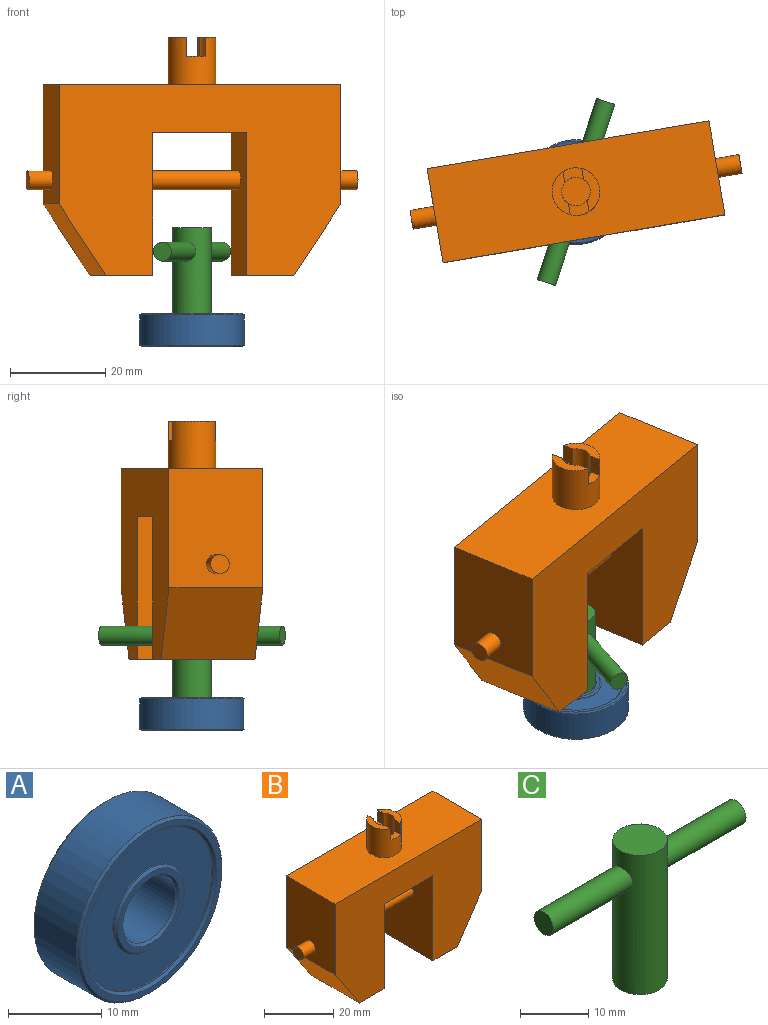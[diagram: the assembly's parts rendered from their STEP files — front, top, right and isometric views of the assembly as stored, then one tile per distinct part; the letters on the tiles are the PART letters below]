
ASSEMBLY  parts=3 mates=2
PART A: 20 faces, bbox 22x7x22 mm
  f0: cylinder r=9.7mm len=19.4mm, axis (0,1,0), area 12.2mm2, adj f11,f14
  f1: cylinder r=9.7mm len=19.4mm, axis (0,1,0), area 12.2mm2, adj f10,f18
  f2: cylinder r=11mm len=22mm, axis (0,1,0), area 442.3mm2, adj f15,f19
  f3: plane 21.4x21.4mm, normal (0,-1,0), area 45.5mm2, adj f18,f19
  f4: plane 21.4x21.4mm, normal (0,1,0), area 45.5mm2, adj f14,f15
  f5: cylinder r=5.3mm len=10.6mm, axis (0,1,0), area 6.7mm2, adj f11,f13
  f6: cylinder r=4mm len=8mm, axis (0,1,0), area 160.8mm2, adj f12,f16
  f7: cylinder r=5.3mm len=10.6mm, axis (0,1,0), area 6.7mm2, adj f10,f17
  f8: plane 10x10mm, normal (0,-1,0), area 20.5mm2, adj f16,f17
  f9: plane 10x10mm, normal (0,1,0), area 20.5mm2, adj f12,f13
  f10: plane 19.4x19.4mm, normal (0,-1,0), area 207.3mm2, adj f1,f7
  f11: plane 19.4x19.4mm, normal (0,1,0), area 207.3mm2, adj f0,f5
  f12: cone r=4.3mm half-angle=45deg, axis (0,1,0), area 11.1mm2, adj f6,f9
  f13: cone r=5.3mm half-angle=45deg, axis (0,-1,0), area 13.7mm2, adj f5,f9
  f14: cone r=10mm half-angle=45deg, axis (0,1,0), area 26.3mm2, adj f0,f4
  f15: cone r=11mm half-angle=45deg, axis (0,-1,0), area 28.9mm2, adj f2,f4
  f16: cone r=4mm half-angle=45deg, axis (0,-1,0), area 11.1mm2, adj f6,f8
  f17: cone r=5mm half-angle=45deg, axis (0,1,0), area 13.7mm2, adj f7,f8
  f18: cone r=9.7mm half-angle=45deg, axis (0,-1,0), area 26.3mm2, adj f1,f3
  f19: cone r=10.7mm half-angle=45deg, axis (0,1,0), area 28.9mm2, adj f2,f3
PART B: 28 faces, bbox 70x20x50 mm
  f0: cylinder r=3mm len=10mm, axis (0,0,-1), area 153.5mm2, adj f2,f20,f21,f22,f23,f24,f25,f26
  f1: cylinder r=5mm len=10mm, axis (0,0,-1), area 281.2mm2, adj f2,f10,f20,f22,f23,f24,f25,f26
  f2: plane 9.17x3mm, normal (0,0,1), area 16.7mm2, adj f0,f1,f24,f26
  f3: plane 20x10mm, normal (0,0,-1), area 200mm2, adj f4,f12,f13,f14
  f4: plane 30x20mm, normal (1,0,0), area 587.4mm2, adj f3,f5,f13,f14,f19
  f5: plane 20x20mm, normal (0,0,-1), area 400mm2, adj f4,f6,f13,f14
  f6: plane 30x20mm, normal (-1,0,0), area 587.4mm2, adj f5,f7,f13,f14,f19
  f7: plane 20x10mm, normal (0,0,-1), area 200mm2, adj f6,f8,f13,f14
  f8: plane 20x15mm, normal (0.83,0,-0.55), area 360.6mm2, adj f7,f9,f13,f14
  f9: plane 25x20mm, normal (1,0,0), area 487.4mm2, adj f8,f10,f13,f14,f18
  f10: plane 60x20mm, normal (0,0,1), area 1121.5mm2, adj f1,f9,f11,f13,f14
  f11: plane 25x20mm, normal (-1,0,0), area 487.4mm2, adj f10,f12,f13,f14,f16
  f12: plane 20x15mm, normal (-0.83,0,-0.55), area 360.6mm2, adj f3,f11,f13,f14
  f13: plane 60x40mm, normal (0,-1,0), area 1650mm2, adj f3,f4,f5,f6,f7,f8,f9,f10
  f14: plane 60x40mm, normal (0,1,0), area 1650mm2, adj f3,f4,f5,f6,f7,f8,f9,f10
  f15: plane 4x4mm, normal (-1,0,0), area 12.6mm2, adj f16
  f16: cylinder r=2mm len=5mm, axis (1,0,0), area 62.8mm2, adj f11,f15
  f17: plane 4x4mm, normal (1,0,0), area 12.6mm2, adj f18
  f18: cylinder r=2mm len=5mm, axis (1,0,0), area 62.8mm2, adj f9,f17
  f19: cylinder r=2mm len=20mm, axis (1,0,0), area 251.3mm2, adj f4,f6
  f20: plane 9.17x3mm, normal (0,0,1), area 16.7mm2, adj f0,f1,f22,f27
  f21: plane 6x6mm, normal (0,0,1), area 28.3mm2, adj f0
  f22: plane 4x2.35mm, normal (-1,0,0), area 9.4mm2, adj f0,f1,f20,f23
  f23: plane 4x2.76mm, normal (0,0,1), area 8.4mm2, adj f0,f1,f22,f24
  f24: plane 4x2.35mm, normal (1,0,0), area 9.4mm2, adj f0,f1,f2,f23
  f25: plane 4x2.76mm, normal (0,0,1), area 8.4mm2, adj f0,f1,f26,f27
  f26: plane 4x2.35mm, normal (1,0,0), area 9.4mm2, adj f0,f1,f2,f25
  f27: plane 4x2.35mm, normal (-1,0,0), area 9.4mm2, adj f0,f1,f20,f25
PART C: 7 faces, bbox 40x8x25 mm
  f0: cylinder r=4mm len=25mm, axis (0,0,-1), area 602.3mm2, adj f1,f2,f4,f5
  f1: plane 8x8mm, normal (0,0,1), area 50.3mm2, adj f0
  f2: plane 8x8mm, normal (0,0,-1), area 50.3mm2, adj f0
  f3: plane 4x4mm, normal (1,0,0), area 12.6mm2, adj f4
  f4: cylinder r=2mm len=16.54mm, axis (-1,0,0), area 204.4mm2, adj f0,f3
  f5: cylinder r=2mm len=16.54mm, axis (-1,0,0), area 204.4mm2, adj f0,f6
  f6: plane 4x4mm, normal (-1,0,0), area 12.6mm2, adj f5
PLACE A rot(axis=(1,0,0),90deg) t=(-42.39,-5.81,2.82)mm fixed
PLACE B rot(axis=(0,0,1),9.6deg) t=(-44.07,4.05,14.32)mm
PLACE C rot(axis=(0,0,-1),108.1deg) t=(-42.39,-5.81,-0.68)mm
MATE cylindrical B.f0 <-> C.f0  axis (0,0,1) through (-42.39,-5.81,54.32)mm
MATE revolute C.f0 <-> A.f0  axis (0,0,-1) through (-42.39,-5.81,-0.68)mm
